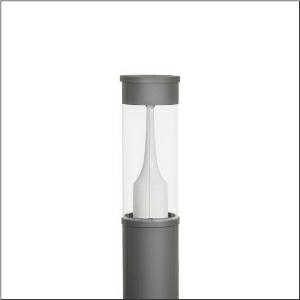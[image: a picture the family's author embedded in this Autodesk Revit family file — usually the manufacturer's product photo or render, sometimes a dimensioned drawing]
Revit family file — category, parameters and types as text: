
# Revit family: city-light_120_iq___p1_0a_5xa5285bf14h_8c15
name_source: partatom
category: Lighting Fixtures
units: mm (PartAtom-declared; Revit-internal decimal feet)

## family parameters
Cut with Voids When Loaded = No
Host = Face
Light Source = No
Part Type = Normal
Room Calculation Point = No
Round Connector Dimension = Use Diameter
Shared = No

## types (1)
- --- (1 x LED, 1510 lm, 12.9 W, 2200K)
    Apparent Load = 13 VA
    CIE Flux Codes = 32 61 90 93 100
    Color Rendering = 70
    Color Temperature = 2200K
    Default Elevation = 1800 mm
    Description = City-Light 120 iQ, bollard luminaire, Module 540 iQ-SR, primary light control with 3 zone facetted reflector, of plastic, silver coated, highly specular, structured, primary optical cover: cover, of PMMA, transparent, partly coated, light distribution: P1.0a, primary light characteristic: strongly asymmetric, LED, High Power LED, rated luminous flux: 1.510lm, luminous efficacy: 117lm/W, light colour: 722, colour temperature: 2200K, control gear: iQ Street-Remote, control: pre-setting: logarithmic dimming characteristic, Street-Remote, Auto-Match, Temp-Guard, Lumen-Switch, Night-Set, Smart-Wire, Light-Fading, Desk-Remote (wireless, voltage-free reading and setting of iQ features in the workshop via application-optimized NFC function/RFID function), optimised constant luminous flux control (CLO 2.0), with terminal, 6-pole, max. 2.5mm², mains connection: 230..240V, AC, 50/60Hz, start of lifetime: 13W, end of service life: 13W, reduction: 6W, luminaire housing, cylindrical, of extruded aluminium section, coated, Siteco® metallic grey (DB 702S), length: 1.200mm, diameter: 200mm, Module 540 iQ-SR, traffic white (RAL 9016), equipment: standard, protection rating (complete): IP54, insulation class (complete): insulation class II (safety insulation), certification: CE, ENEC, VDE, packaging unit: 1 piece

Light Distribution: P1.0a
    Height = 500 mm
    Lamp = 1 x LED
    Lamp Light Flux = 1510 lm
    Lamp Power = 12.9 W
    Lamp count = 1
    Length = 200 mm  [stored 0.656168 ft]
    Luminous efficacy = 117 lm/W
    Manufacturer = Siteco
    ModVariant = No
    Model = 5XA5285BF14H
    Mounting Place = Floor
    Mounting Type = Freestanding
    Number of Poles = 1
    OnlyDefault = Yes
    Power Factor = 1
    Product Name = City-Light 120 iQ | P1.0a
    Product group = bollard luminaire
    ProductGroupID = 1304
    Protection Class = Protection class II
    Protection Degree = IP 54
    RLX_Detail_Level = 1
    RLX_Emergency_Light_Flux = 0 lm
    RLX_Emergency_Type = 0
    RLX_Emergency_Type_DB = No
    RlxData = <blob elided: 52645 chars, md5=49731e52>
    Socket = socket
    Standby Power = 0 W
    System Light Flux = 1510 lm
    System Power = 13 W
    Type Comments = factory setting: luminous flux: 100 % | dim-lin: 254 | 516 mA
    Type Image = l_1006922.jpg
    URL = http://relux.com
    VarID = @adj_159105
    Voltage = 0 V
    Weight = 0.00 kg
    Width = 0 mm  [stored 0 ft]

note: [stored X ft] marks values corroborated as IEEE doubles in the binary element streams (Revit-internal decimal feet)

## geometry (parser evidence)
native form markers: Blend x4, Sweep x10
no freeform markers — native parametric forms only
